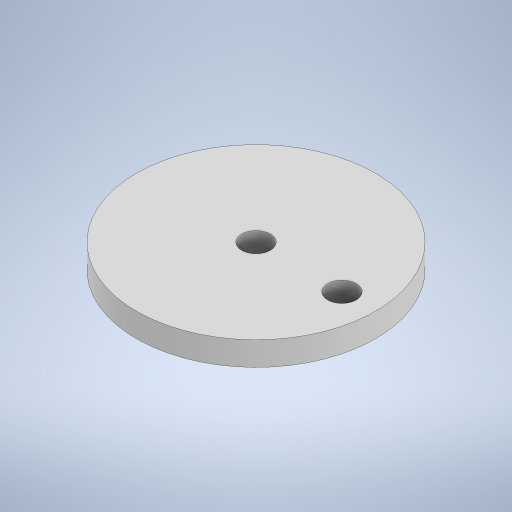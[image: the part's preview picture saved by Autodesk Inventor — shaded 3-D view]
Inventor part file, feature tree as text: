
AUTODESK INVENTOR PART (.ipt)
format: ipt  version: 2023 (Build 270158000, 158)  size: 218,624 bytes
history: native  units: in
note: dims shown in document units (in); Inventor stores cm internally (conversion verified against a paired STEP export)
features: sketch x4, extrude x3
ambient origin geometry x8: Origin, YZ Plane, XZ Plane, XY Plane, X Axis, Y Axis, Z Axis, Center Point
bodies: Solid1 (feature_tree)
feature tree (7):
  sketch  "Sketch1"  dims[d0=1.9685in d1=0.1969in d2=0.0in]
  sketch  "Sketch2"  dims[d3=0.2362in d4=0.1969in d5=0.0in]
  extrude  "Extrusion1"  Depth=0.1969in TaperAngle=0.0deg
  extrude  "Extrusion2"  Depth=0.1969in TaperAngle=0.0deg
  extrude  "Extrusion3"  Depth=0.1969in TaperAngle=0.0deg
  sketch  "Sketch3"  dims[d6=0.2362in d7=0.1969in d8=0.0in]
  sketch  "Sketch4"
